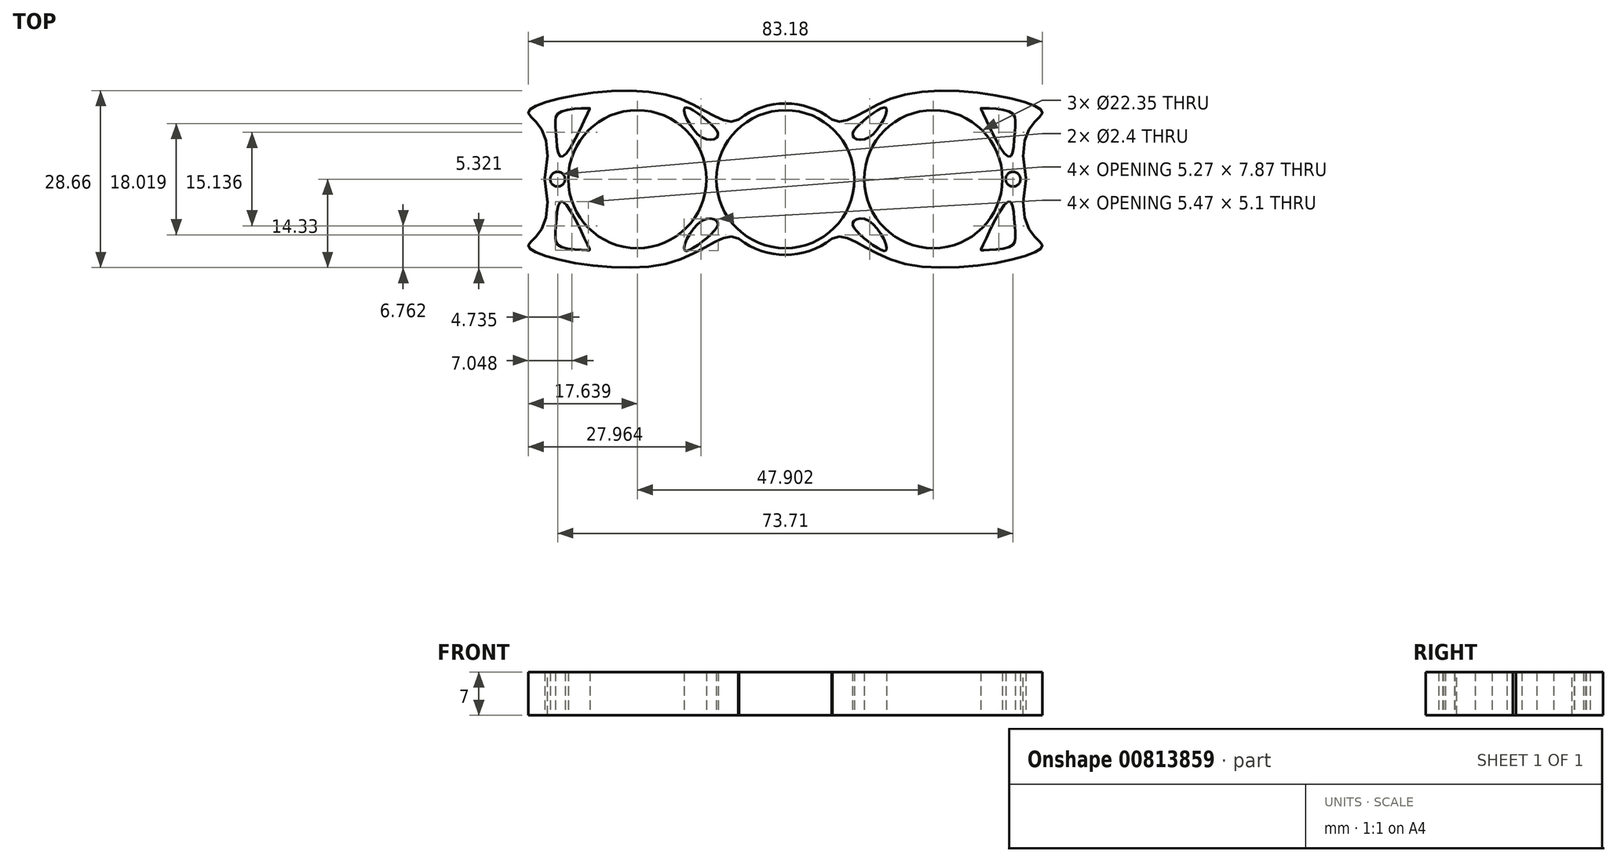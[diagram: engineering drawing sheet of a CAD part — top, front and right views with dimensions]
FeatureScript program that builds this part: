
annotation { "Feature Type Name" : "Feature", "Feature Type Description" : "" }
export const myFeature = defineFeature(function(context is Context, id is Id, definition is map)
    precondition{}
    {
        {
            var Q0;
            Q0=qCreatedBy(makeId("Top.planeOp"),FACE);
            var sketch = newSketch(context, id + "F0", { "sketchPlane" : qUnion([Q0])});
            skCircle(sketch, "E0", {"center": v(0, 0) * mm, "radius": 11.18 * mm});
            skCircle(sketch, "E1", {"center": v(0, 0) * mm, "radius": 12.25 * mm});
            skLineSegment(sketch, "E2", {"start": v(0, 0) * mm, "end": v(-38.99, 0) * mm});
            skFitSpline(sketch, "E3", {"points": [v(-7.53, 9.67) * mm, v(-19.11, 13.65) * mm, v(-41.53, 11.05) * mm, v(-38.99, 0) * mm], "startDerivative": vector(-25.79, -15.64) * mm, "endDerivative": vector(-23.02, -94.15) * mm});
            skFitSpline(sketch, "E4.MirrorCS", {"points": [v(-7.53, -9.67) * mm, v(-19.11, -13.65) * mm, v(-41.53, -11.05) * mm, v(-38.99, 0) * mm], "startDerivative": vector(-25.79, 15.64) * mm, "endDerivative": vector(-23.02, 94.15) * mm});
            skFitSpline(sketch, "E5.MirrorCS", {"points": [v(7.53, 9.67) * mm, v(19.11, 13.65) * mm, v(41.53, 11.05) * mm, v(38.99, 0) * mm], "startDerivative": vector(25.79, -15.64) * mm, "endDerivative": vector(23.02, -94.15) * mm});
            skFitSpline(sketch, "E6.MirrorCS", {"points": [v(7.53, -9.67) * mm, v(19.11, -13.65) * mm, v(41.53, -11.05) * mm, v(38.99, 0) * mm], "startDerivative": vector(25.79, 15.64) * mm, "endDerivative": vector(23.02, 94.15) * mm});
            skCircle(sketch, "E7", {"center": v(-23.95, 0) * mm, "radius": 11.18 * mm});
            skCircle(sketch, "E8.MirrorC", {"center": v(23.95, 0) * mm, "radius": 11.18 * mm});
            skFitSpline(sketch, "E9", {"points": [v(-36.05, -3.64) * mm, v(-37.14, -7.91) * mm, v(-36.36, -10.91) * mm, v(-31.63, -11.5) * mm, v(-31.63, -11.5) * mm, v(-36.05, -3.64) * mm]});
            skFitSpline(sketch, "E10.MirrorC", {"points": [v(-36.05, 3.64) * mm, v(-37.14, 7.91) * mm, v(-36.36, 10.91) * mm, v(-31.63, 11.5) * mm, v(-31.63, 11.5) * mm, v(-36.05, 3.64) * mm]});
            skFitSpline(sketch, "E11", {"points": [v(-13.5, -6.76) * mm, v(-10.93, -6.98) * mm, v(-12.77, -9.56) * mm, v(-16.31, -11.5) * mm, v(-13.5, -6.76) * mm]});
            skFitSpline(sketch, "E12.MirrorC", {"points": [v(-13.5, 6.76) * mm, v(-10.93, 6.98) * mm, v(-12.77, 9.56) * mm, v(-16.31, 11.5) * mm, v(-13.5, 6.76) * mm]});
            skFitSpline(sketch, "E13.MirrorC", {"points": [v(13.5, 6.76) * mm, v(10.93, 6.98) * mm, v(12.77, 9.56) * mm, v(16.31, 11.5) * mm, v(13.5, 6.76) * mm]});
            skFitSpline(sketch, "E14.MirrorC", {"points": [v(36.05, 3.64) * mm, v(37.14, 7.91) * mm, v(36.36, 10.91) * mm, v(31.63, 11.5) * mm, v(31.63, 11.5) * mm, v(36.05, 3.64) * mm]});
            skFitSpline(sketch, "E15.MirrorC", {"points": [v(36.05, -3.64) * mm, v(37.14, -7.91) * mm, v(36.36, -10.91) * mm, v(31.63, -11.5) * mm, v(31.63, -11.5) * mm, v(36.05, -3.64) * mm]});
            skFitSpline(sketch, "E16.MirrorC", {"points": [v(13.5, -6.76) * mm, v(10.93, -6.98) * mm, v(12.77, -9.56) * mm, v(16.31, -11.5) * mm, v(13.5, -6.76) * mm]});
            skCircle(sketch, "E17", {"center": v(36.85, 0) * mm, "radius": 1.2 * mm});
            skCircle(sketch, "E18.MirrorC", {"center": v(-36.85, 0) * mm, "radius": 1.2 * mm});
            skSolve(sketch);
        }
        {
            var Q0;
            Q0 = qSketchRegion(id + "F0", true);
            extrude(context, id + "F1", {"entities" : qUnion([Q0]), "depth" : 7 * mm, "offsetDistance" : 25.4 * mm});
        }
        {
            var Q0;
            Q0=makeQuery(id+"F1.opExtrude","SWEPT_EDGE",EDGE,{"disambiguationData":[OSD([sQuery(id+"F0.wireOp",EDGE,"E2"),sQuery(id+"F0.wireOp",EDGE,"E3"),sQuery(id+"F0.wireOp",EDGE,"E4.MirrorCS")])]});
            var Q1;
            Q1=makeQuery(id+"F1.opExtrude","SWEPT_EDGE",EDGE,{"disambiguationData":[OSD([sQuery(id+"F0.wireOp",EDGE,"E1"),sQuery(id+"F0.wireOp",EDGE,"E4.MirrorCS")])]});
            var Q2;
            Q2=makeQuery(id+"F1.opExtrude","SWEPT_EDGE",EDGE,{"disambiguationData":[OSD([sQuery(id+"F0.wireOp",EDGE,"E1"),sQuery(id+"F0.wireOp",EDGE,"E6.MirrorCS")])]});
            var Q3;
            Q3=makeQuery(id+"F1.opExtrude","SWEPT_EDGE",EDGE,{"disambiguationData":[OSD([sQuery(id+"F0.wireOp",EDGE,"E5.MirrorCS"),sQuery(id+"F0.wireOp",EDGE,"E6.MirrorCS")])]});
            var Q4;
            Q4=makeQuery(id+"F1.opExtrude","SWEPT_EDGE",EDGE,{"disambiguationData":[OSD([sQuery(id+"F0.wireOp",EDGE,"E1"),sQuery(id+"F0.wireOp",EDGE,"E3")])]});
            var Q5;
            Q5=makeQuery(id+"F1.opExtrude","SWEPT_EDGE",EDGE,{"disambiguationData":[OSD([sQuery(id+"F0.wireOp",EDGE,"E1"),sQuery(id+"F0.wireOp",EDGE,"E5.MirrorCS")])]});
            chamfer(context, id + "F2", {"entities" : qUnion([Q0, Q1, Q2, Q3, Q4, Q5]), "width" : 1 * mm, "tangentPropagation" : true});
        }
    });
